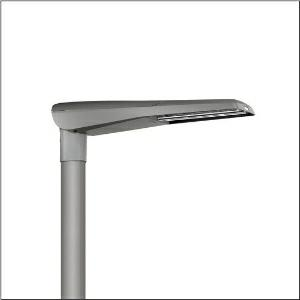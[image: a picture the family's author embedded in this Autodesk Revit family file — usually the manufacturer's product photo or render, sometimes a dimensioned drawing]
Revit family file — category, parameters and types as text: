
# Revit family: streetlight_sl_11_iq_mini___st0_5a_5xc2bc1f08he_0989
name_source: partatom
category: Lighting Fixtures
units: mm (PartAtom-declared; Revit-internal decimal feet)

## family parameters
Cut with Voids When Loaded = No
Host = Face
Light Source = No
Part Type = Normal
Room Calculation Point = No
Round Connector Dimension = Use Diameter
Shared = No

## types (1)
- --- (1 x LED, 6780 lm, 63.6 W, 2200K)
    Apparent Load = 64 VA
    CIE Flux Codes = 43 74 97 100 100
    Color Rendering = 70
    Color Temperature = 2200K
    Default Elevation = 1800 mm
    Description = Streetlight SL 11 iQ mini, mast luminaire, primary light control with 3 zone facetted reflector, of plastic, silver coated, highly specular, primary optical cover: cover, of PMMA, transparent, light distribution: ST0.5a, light emission: direct distribution, primary light characteristic: asymmetric, installation type: post-top, side-entry, lamps: LED, High Power LED, rated values: 8.280lm | 62,2W | 133,1lm/W (begin service life); end service life: 8.280lm | 65,6W; at 50% lumin. flux: 4.140lm | 29,4W | 140,8lm/W, colour temperature: 2200/2700/3000/4000K, colour rendering: CRI > 70, light colour: 722/727/730/740, light setting 1 begin service life: 100% | 8.280lm | 62,2W | 133,1lm/W | 3.000K, light setting 1 end service life: 65,6W, further light settings possible, control: Street-Remote, Auto-Match, Temp-Guard, Lumen-Switch, Night-Set, Smart-Wire, Light-Fading, Desk-Remote (wireless, voltage-free reading and setting of iQ features in the workshop via application-optimized NFC function/RFID function), optimised constant luminous flux control (CLO 2.0), with cable H07RN-F 5x 1.5mm², mains connection: 230..240V, AC, 50/60Hz, connection cable pre-assembled, cable length: 8,5m, luminaire housing, of diecast aluminium, powder-coated, Siteco® metallic grey (DB 702S), please order mast flange separately, inclination adjustable without tools: 0°, 5°, 10°, 15° (post-top) | 0°, -5°, -10°, -15° (side-entry), sealing non-destructively replaceable, multi-level sealing system, length: 736mm, width: 174mm, height: 116mm, mast flange for spigot size: 42mm (side-entry): 5XC10008XM4, 60/48mm (side-entry/post-top): 5XC10108XM2, 76/60mm (side-entry/post-top): 5XC10108XM1, equipment: Power, protection rating (complete): IP66, insulation class (complete): insulation class II (safety insulation), certification: CE, ENEC, ENEC+, VDE, impact resistance: IK10, permissible operating ambient temperature for outdoor applications: -25..+50°C, standard-compliant lighting for roads and squares, Environmental Product Declaration (EPD) tested and certified by an independent institute, packaging unit: 1 piece

Light Distribution: ST0.5a
    Height = 116 mm
    Lamp = 1 x LED
    Lamp Light Flux = 6780 lm
    Lamp Power = 63.6 W
    Lamp count = 1
    Length = 736 mm
    Luminous efficacy = 107 lm/W
    Manufacturer = Siteco
    ModVariant = No
    Model = 5XC2BC1F08HE
    Number of Poles = 1
    OnlyDefault = Yes
    Power Factor = 1
    Product Name = Streetlight SL 11 iQ mini | ST0.5a
    Product group = mast luminaire | pylon top
    ProductGroupID = 6100
    Protection Class = Protection class II
    Protection Degree = IP 66
    RLX_Detail_Level = 1
    RLX_Emergency_Light_Flux = 0 lm
    RLX_Emergency_Type = 0
    RLX_Emergency_Type_DB = No
    RlxData = <blob elided: 58377 chars, md5=d7214739>
    Socket = socket
    Standby Power = 0 W
    System Light Flux = 6780 lm
    System Power = 64 W
    Type Comments = individual setting: luminous flux: 100 % | dim-lin: 254 | 866 mA
    Type Image = l_1003508.jpg
    URL = http://relux.com
    VarID = @adj_056165
    Voltage = 0 V
    Weight = 0.00 kg
    Width = 174 mm

## geometry (parser evidence)
native form markers: Blend x4, Sweep x12
no freeform markers — native parametric forms only
